# Revit family: WWW_A3-Full-Arch-1530-CHC4
name_source: partatom
category: Windows
revit_build: Autodesk Revit 2016 (Build: 20150220_1215(x64)
units: mm (PartAtom-declared; Revit-internal decimal feet)

## family parameters
Always vertical = Yes
Cut with Voids When Loaded = No
Host = Wall
Room Calculation Point = No
Shared = No

## types (2) — shared parameters
Assembly Code = B2020130
Default Sill Height = 770 mm  [stored 2.52625 ft]
Frame Material = Frame Material
Head height = 2300 mm
Height = 1530 mm  [stored 5.01969 ft]
Manufacturer = AC Shopfitters (Windows)
Manufacturer Code = CHC4
Model = Full Arch
Type Comments = series iv frame profile
URL = www.acdoors.co.za
Wall Closure = By host
zero-valued in all types: Rough Height

## per-type parameters (varying)
| type | Rough Width | Width |
| 1530 x 1116 CHC4 | 1898 mm  [stored 6.22703 ft] | 1116 mm |
| 1530 x 0580 CHC4 | 0 mm  [stored 0 ft] | 580 mm  [stored 1.90289 ft] |

note: [stored X ft] marks values corroborated as IEEE doubles in the binary element streams (Revit-internal decimal feet)

## geometry (parser evidence)
native form markers: Sweep x6
no freeform markers — native parametric forms only
